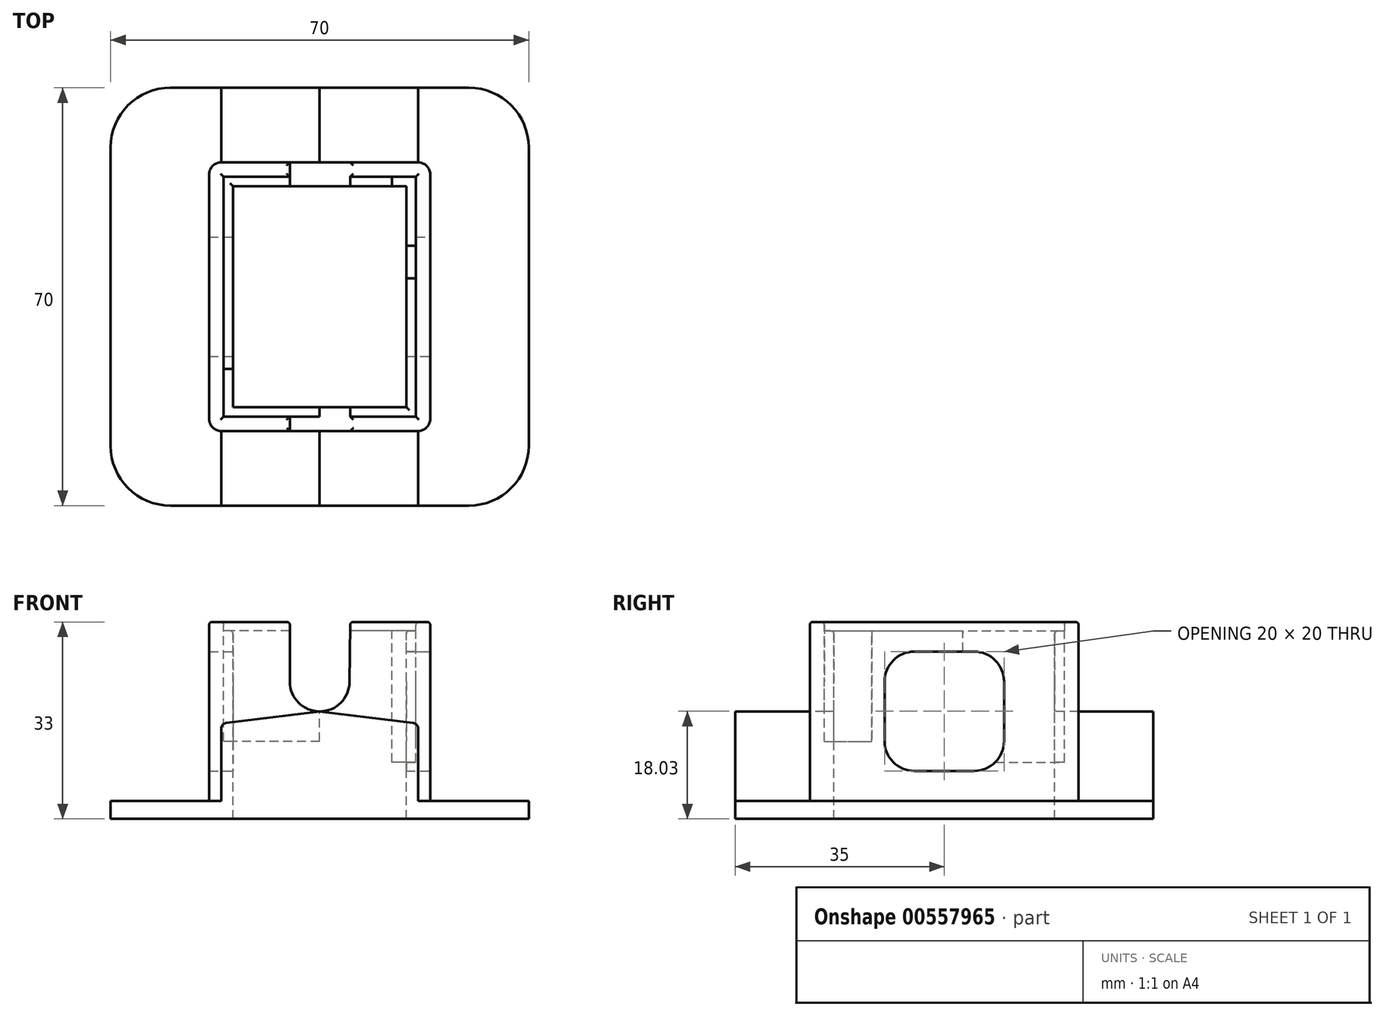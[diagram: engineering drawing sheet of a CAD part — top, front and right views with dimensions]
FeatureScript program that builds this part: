
annotation { "Feature Type Name" : "Feature", "Feature Type Description" : "" }
export const myFeature = defineFeature(function(context is Context, id is Id, definition is map)
    precondition{}
    {
        {
            var Q0;
            Q0=qCreatedBy(makeId("Top.planeOp"),FACE);
            var sketch = newSketch(context, id + "F0", { "sketchPlane" : qUnion([Q0])});
            skLineSegment(sketch, "E0.bottom", {"start": v(25, -35) * mm, "end": v(-25, -35) * mm});
            skLineSegment(sketch, "E0.top", {"start": v(25, 35) * mm, "end": v(-25, 35) * mm});
            skLineSegment(sketch, "E0.left", {"start": v(35, -25) * mm, "end": v(35, 25) * mm});
            skLineSegment(sketch, "E0.right", {"start": v(-35, -25) * mm, "end": v(-35, 25) * mm});
            skPoint(sketch, "E0.middle", {"position": v(0, 0) * mm});
            skPoint(sketch, "E1.visualSharp", {"position": v(-35, -35) * mm});
            skArc(sketch, "E1.filletArc", {"start": v(-35, -25) * mm, "mid": v(-32.07, -32.07) * mm, "end": v(-25, -35) * mm});
            skPoint(sketch, "E2.visualSharp", {"position": v(35, -35) * mm});
            skArc(sketch, "E2.filletArc", {"start": v(25, -35) * mm, "mid": v(32.07, -32.07) * mm, "end": v(35, -25) * mm});
            skPoint(sketch, "E3.visualSharp", {"position": v(35, 35) * mm});
            skArc(sketch, "E3.filletArc", {"start": v(35, 25) * mm, "mid": v(32.07, 32.07) * mm, "end": v(25, 35) * mm});
            skPoint(sketch, "E4.visualSharp", {"position": v(-35, 35) * mm});
            skArc(sketch, "E4.filletArc", {"start": v(-25, 35) * mm, "mid": v(-32.07, 32.07) * mm, "end": v(-35, 25) * mm});
            skSolve(sketch);
        }
        {
            var Q0;
            Q0=qSketchRegion(id+"F0",true);
            extrude(context, id + "F1", {"entities" : qUnion([Q0]), "depth" : 3 * mm, "offsetDistance" : 25 * mm});
        }
        {
            var Q0;
            Q0=makeQuery(id+"F1.opExtrude","CAP_FACE",FACE,{"disambiguationData":[OSD([sQuery(id+"F0.wireOp",EDGE,"E0.bottom"),sQuery(id+"F0.wireOp",EDGE,"E0.top"),sQuery(id+"F0.wireOp",EDGE,"E0.left"),sQuery(id+"F0.wireOp",EDGE,"E0.right"),sQuery(id+"F0.wireOp",EDGE,"E1.filletArc"),sQuery(id+"F0.wireOp",EDGE,"E2.filletArc"),sQuery(id+"F0.wireOp",EDGE,"E3.filletArc"),sQuery(id+"F0.wireOp",EDGE,"E4.filletArc")])],"isStart":false});
            var sketch = newSketch(context, id + "F2", { "sketchPlane" : qUnion([Q0])});
            skLineSegment(sketch, "E5.bottom", {"start": v(16.5, -22.5) * mm, "end": v(-16.5, -22.5) * mm});
            skLineSegment(sketch, "E5.top", {"start": v(16.5, 22.5) * mm, "end": v(-16.5, 22.5) * mm});
            skLineSegment(sketch, "E5.left", {"start": v(18.5, -20.5) * mm, "end": v(18.5, 20.5) * mm});
            skLineSegment(sketch, "E5.right", {"start": v(-18.5, -20.5) * mm, "end": v(-18.5, 20.5) * mm});
            skPoint(sketch, "E5.middle", {"position": v(0, 0) * mm});
            skPoint(sketch, "E6.visualSharp", {"position": v(18.5, -22.5) * mm});
            skArc(sketch, "E6.filletArc", {"start": v(16.5, -22.5) * mm, "mid": v(17.91, -21.91) * mm, "end": v(18.5, -20.5) * mm});
            skPoint(sketch, "E7.visualSharp", {"position": v(18.5, 22.5) * mm});
            skArc(sketch, "E7.filletArc", {"start": v(18.5, 20.5) * mm, "mid": v(17.91, 21.91) * mm, "end": v(16.5, 22.5) * mm});
            skPoint(sketch, "E8.visualSharp", {"position": v(-18.5, 22.5) * mm});
            skArc(sketch, "E8.filletArc", {"start": v(-16.5, 22.5) * mm, "mid": v(-17.91, 21.91) * mm, "end": v(-18.5, 20.5) * mm});
            skPoint(sketch, "E9.visualSharp", {"position": v(-18.5, -22.5) * mm});
            skArc(sketch, "E9.filletArc", {"start": v(-18.5, -20.5) * mm, "mid": v(-17.91, -21.91) * mm, "end": v(-16.5, -22.5) * mm});
            skSolve(sketch);
        }
        {
            var Q0;
            Q0=makeQuery(id+"F2.imprint","IMPRINT",FACE,{"disambiguationData":[TD([[makeQuery(id+"F2.imprint","IMPRINT",EDGE,{"derivedFrom":sQuery(id+"F2.wireOp",EDGE,"E5.bottom")}),-1.0]])]});
            extrude(context, id + "F3", {"entities" : qUnion([Q0]), "operationType" : NewBodyOperationType.ADD, "depth" : 30 * mm, "offsetDistance" : 25 * mm});
        }
        {
            var Q0;
            Q0=makeQuery(id+"F3.opExtrude","CAP_FACE",FACE,{"disambiguationData":[OSD([sQuery(id+"F2.wireOp",EDGE,"E5.bottom"),sQuery(id+"F2.wireOp",EDGE,"E5.top"),sQuery(id+"F2.wireOp",EDGE,"E5.left"),sQuery(id+"F2.wireOp",EDGE,"E5.right"),sQuery(id+"F2.wireOp",EDGE,"E6.filletArc"),sQuery(id+"F2.wireOp",EDGE,"E7.filletArc"),sQuery(id+"F2.wireOp",EDGE,"E8.filletArc"),sQuery(id+"F2.wireOp",EDGE,"E9.filletArc")])],"isStart":false});
            var sketch = newSketch(context, id + "F4", { "sketchPlane" : qUnion([Q0])});
            skLineSegment(sketch, "E10.bottom", {"start": v(-14.5, 18.5) * mm, "end": v(14.5, 18.5) * mm});
            skLineSegment(sketch, "E10.top", {"start": v(-14.5, -18.5) * mm, "end": v(14.5, -18.5) * mm});
            skLineSegment(sketch, "E10.left", {"start": v(-14.5, 18.5) * mm, "end": v(-14.5, -18.5) * mm});
            skLineSegment(sketch, "E10.right", {"start": v(14.5, 18.5) * mm, "end": v(14.5, -18.5) * mm});
            skPoint(sketch, "E10.middle", {"position": v(0, 0) * mm});
            skSolve(sketch);
        }
        {
            var Q0;
            Q0=makeQuery(id+"F4.imprint","IMPRINT",FACE,{"disambiguationData":[TD([[makeQuery(id+"F4.imprint","IMPRINT",EDGE,{"derivedFrom":sQuery(id+"F4.wireOp",EDGE,"E10.bottom")}),-1.0]])]});
            extrude(context, id + "F5", {"entities" : qUnion([Q0]), "operationType" : NewBodyOperationType.REMOVE, "endBound" : BoundingType.THROUGH_ALL, "oppositeDirection" : true, "depth" : 25 * mm});
        }
        {
            var Q0;
            Q0=makeQuery(id+"F3.opExtrude","CAP_FACE",FACE,{"disambiguationData":[OSD([sQuery(id+"F2.wireOp",EDGE,"E5.bottom"),sQuery(id+"F2.wireOp",EDGE,"E5.top"),sQuery(id+"F2.wireOp",EDGE,"E5.left"),sQuery(id+"F2.wireOp",EDGE,"E5.right"),sQuery(id+"F2.wireOp",EDGE,"E6.filletArc"),sQuery(id+"F2.wireOp",EDGE,"E7.filletArc"),sQuery(id+"F2.wireOp",EDGE,"E8.filletArc"),sQuery(id+"F2.wireOp",EDGE,"E9.filletArc")])],"isStart":false});
            var sketch = newSketch(context, id + "F6", { "sketchPlane" : qUnion([Q0])});
            skLineSegment(sketch, "E11.bottom", {"start": v(16.1, -20.1) * mm, "end": v(-16.1, -20.1) * mm});
            skLineSegment(sketch, "E11.top", {"start": v(16.1, 20.1) * mm, "end": v(-16.1, 20.1) * mm});
            skLineSegment(sketch, "E11.left", {"start": v(16.1, -20.1) * mm, "end": v(16.1, 20.1) * mm});
            skLineSegment(sketch, "E11.right", {"start": v(-16.1, -20.1) * mm, "end": v(-16.1, 20.1) * mm});
            skPoint(sketch, "E11.middle", {"position": v(0, 0) * mm});
            skSolve(sketch);
        }
        {
            var Q0;
            Q0=qSketchRegion(id+"F6",true);
            extrude(context, id + "F7", {"entities" : qUnion([Q0]), "operationType" : NewBodyOperationType.REMOVE, "oppositeDirection" : true, "depth" : 1.5 * mm});
        }
        {
            var Q0;
            Q0=makeQuery(id+"F7.boolean.opBoolean","COPY",FACE,{"derivedFrom":makeQuery(id+"F7.opExtrude","CAP_FACE",FACE,{"disambiguationData":[OSD([sQuery(id+"F6.wireOp",EDGE,"E11.bottom"),sQuery(id+"F6.wireOp",EDGE,"E11.top"),sQuery(id+"F6.wireOp",EDGE,"E11.left"),sQuery(id+"F6.wireOp",EDGE,"E11.right")])],"isStart":false})});
            var sketch = newSketch(context, id + "F8", { "sketchPlane" : qUnion([Q0])});
            skLineSegment(sketch, "E12.bottom", {"start": v(12.1, 20.1) * mm, "end": v(16.1, 20.1) * mm});
            skLineSegment(sketch, "E12.top", {"start": v(12.1, 3.1) * mm, "end": v(16.1, 3.1) * mm});
            skLineSegment(sketch, "E12.left", {"start": v(12.1, 20.1) * mm, "end": v(12.1, 3.1) * mm});
            skLineSegment(sketch, "E12.right", {"start": v(16.1, 20.1) * mm, "end": v(16.1, 3.1) * mm});
            skSolve(sketch);
        }
        {
            var Q0;
            {var subQ0=sQuery(id+"F8.wireOp",EDGE,"E12.right");var subQ1=sQuery(id+"F8.wireOp",EDGE,"E12.top");var subQ2=makeQuery(id+"F8.imprint","INTERSECT",VERTEX,{"derivedFrom":[subQ1,subQ0]});Q0=makeQuery(id+"F8.imprint","IMPRINT",FACE,{"disambiguationData":[TD([[makeQuery(id+"F8.imprint","IMPRINT",EDGE,{"disambiguationData":[TD([[subQ2,1.0]])],"derivedFrom":subQ1}),1.0]])]});}
            var Q1;
            {var subQ1=sQuery(id+"F8.wireOp",EDGE,"E12.bottom");Q1=makeQuery(id+"F8.imprint","IMPRINT",FACE,{"disambiguationData":[TD([[makeQuery(id+"F8.imprint","IMPRINT",EDGE,{"derivedFrom":subQ1}),1.0]])]});}
            extrude(context, id + "F9", {"entities" : qUnion([Q0, Q1]), "operationType" : NewBodyOperationType.REMOVE, "oppositeDirection" : true, "depth" : 22 * mm});
        }
        {
            var Q0;
            Q0=makeQuery(id+"F3.opExtrude","CAP_FACE",FACE,{"disambiguationData":[OSD([sQuery(id+"F2.wireOp",EDGE,"E5.bottom"),sQuery(id+"F2.wireOp",EDGE,"E5.top"),sQuery(id+"F2.wireOp",EDGE,"E5.left"),sQuery(id+"F2.wireOp",EDGE,"E5.right"),sQuery(id+"F2.wireOp",EDGE,"E6.filletArc"),sQuery(id+"F2.wireOp",EDGE,"E7.filletArc"),sQuery(id+"F2.wireOp",EDGE,"E8.filletArc"),sQuery(id+"F2.wireOp",EDGE,"E9.filletArc")])],"isStart":false});
            var sketch = newSketch(context, id + "F10", { "sketchPlane" : qUnion([Q0])});
            skLineSegment(sketch, "E13.bottom", {"start": v(0, -20.1) * mm, "end": v(-16.1, -20.1) * mm});
            skLineSegment(sketch, "E13.top", {"start": v(0, -12.1) * mm, "end": v(-16.1, -12.1) * mm});
            skLineSegment(sketch, "E13.left", {"start": v(0, -20.1) * mm, "end": v(0, -12.1) * mm});
            skLineSegment(sketch, "E13.right", {"start": v(-16.1, -20.1) * mm, "end": v(-16.1, -12.1) * mm});
            skSolve(sketch);
        }
        {
            var Q0;
            Q0=qSketchRegion(id+"F10",true);
            extrude(context, id + "F11", {"entities" : qUnion([Q0]), "operationType" : NewBodyOperationType.REMOVE, "oppositeDirection" : true, "depth" : 20 * mm, "offsetDistance" : 25 * mm});
        }
        {
            var Q0;
            Q0=makeQuery(id+"F3.opExtrude","SWEPT_FACE",FACE,{"disambiguationData":[OSD([sQuery(id+"F2.wireOp",EDGE,"E5.left")])]});
            var sketch = newSketch(context, id + "F12", { "sketchPlane" : qUnion([Q0])});
            skLineSegment(sketch, "E14.bottom", {"start": v(5, 8.03) * mm, "end": v(-5, 8.03) * mm});
            skLineSegment(sketch, "E14.top", {"start": v(5, 28.03) * mm, "end": v(-5, 28.03) * mm});
            skLineSegment(sketch, "E14.left", {"start": v(10, 13.03) * mm, "end": v(10, 23.03) * mm});
            skLineSegment(sketch, "E14.right", {"start": v(-10, 13.03) * mm, "end": v(-10, 23.03) * mm});
            skPoint(sketch, "E14.middle", {"position": v(0, 18.03) * mm});
            skPoint(sketch, "E15.visualSharp", {"position": v(10, 8.03) * mm});
            skArc(sketch, "E15.filletArc", {"start": v(5, 8.03) * mm, "mid": v(8.54, 9.5) * mm, "end": v(10, 13.03) * mm});
            skPoint(sketch, "E16.visualSharp", {"position": v(-10, 8.03) * mm});
            skArc(sketch, "E16.filletArc", {"start": v(-10, 13.03) * mm, "mid": v(-8.54, 9.5) * mm, "end": v(-5, 8.03) * mm});
            skPoint(sketch, "E17.visualSharp", {"position": v(-10, 28.03) * mm});
            skArc(sketch, "E17.filletArc", {"start": v(-5, 28.03) * mm, "mid": v(-8.54, 26.57) * mm, "end": v(-10, 23.03) * mm});
            skPoint(sketch, "E18.visualSharp", {"position": v(10, 28.03) * mm});
            skArc(sketch, "E18.filletArc", {"start": v(10, 23.03) * mm, "mid": v(8.54, 26.57) * mm, "end": v(5, 28.03) * mm});
            skSolve(sketch);
        }
        {
            var Q0;
            Q0=qSketchRegion(id+"F12",true);
            extrude(context, id + "F13", {"entities" : qUnion([Q0]), "operationType" : NewBodyOperationType.REMOVE, "endBound" : BoundingType.THROUGH_ALL, "oppositeDirection" : true, "depth" : 25 * mm, "offsetDistance" : 25 * mm, "hasSecondDirection" : true, "secondDirectionBound" : BoundingType.THROUGH_ALL, "secondDirectionOppositeDirection" : false, "secondDirectionDepth" : 25 * mm});
        }
        {
            var Q0;
            Q0=makeQuery(id+"F3.opExtrude","SWEPT_FACE",FACE,{"disambiguationData":[OSD([sQuery(id+"F2.wireOp",EDGE,"E5.bottom")])]});
            var sketch = newSketch(context, id + "F14", { "sketchPlane" : qUnion([Q0])});
            skArc(sketch, "E19", {"start": v(-5, 23) * mm, "mid": v(-0.03, 18) * mm, "end": v(5, 22.94) * mm});
            skLineSegment(sketch, "E20", {"start": v(-5, 23) * mm, "end": v(-5, 33) * mm});
            skLineSegment(sketch, "E21", {"start": v(-5, 33) * mm, "end": v(5.11, 33) * mm});
            skLineSegment(sketch, "E22", {"start": v(5.11, 33) * mm, "end": v(5, 22.94) * mm});
            skSolve(sketch);
        }
        {
            var Q0;
            Q0 = qSketchRegion(id + "F14", true);
            extrude(context, id + "F15", {"entities" : qUnion([Q0]), "operationType" : NewBodyOperationType.REMOVE, "endBound" : BoundingType.THROUGH_ALL, "oppositeDirection" : true, "depth" : 25 * mm, "offsetDistance" : 25 * mm});
        }
        {
            var Q0;
            Q0=makeQuery(id+"F3.opExtrude","SWEPT_FACE",FACE,{"disambiguationData":[OSD([sQuery(id+"F2.wireOp",EDGE,"E5.bottom")])]});
            var sketch = newSketch(context, id + "F16", { "sketchPlane" : qUnion([Q0])});
            skLineSegment(sketch, "E23.top", {"start": v(-16.5, 3) * mm, "end": v(16.5, 3) * mm});
            skLineSegment(sketch, "E23.left", {"start": v(-16.5, 15.97) * mm, "end": v(-16.5, 3) * mm});
            skLineSegment(sketch, "E23.right", {"start": v(16.5, 15.97) * mm, "end": v(16.5, 3) * mm});
            skLineSegment(sketch, "E24", {"start": v(0, 18) * mm, "end": v(16.5, 15.97) * mm});
            skLineSegment(sketch, "E25", {"start": v(0, 18) * mm, "end": v(-16.5, 15.97) * mm});
            skSolve(sketch);
        }
        {
            var Q0;
            Q0 = qSketchRegion(id + "F16", true);
            var Q1;
            Q1=makeQuery(id+"F1.opExtrude","SWEPT_FACE",FACE,{"disambiguationData":[OSD([sQuery(id+"F0.wireOp",EDGE,"E0.bottom")])]});
            extrude(context, id + "F17", {"entities" : qUnion([Q0]), "operationType" : NewBodyOperationType.ADD, "endBound" : BoundingType.UP_TO_SURFACE, "depth" : 25 * mm, "endBoundEntityFace" : qUnion([Q1]), "offsetDistance" : 25 * mm});
        }
        {
            var Q0;
            Q0=makeQuery(id+"F3.opExtrude","SWEPT_FACE",FACE,{"disambiguationData":[OSD([sQuery(id+"F2.wireOp",EDGE,"E5.top")])]});
            var sketch = newSketch(context, id + "F18", { "sketchPlane" : qUnion([Q0])});
            skLineSegment(sketch, "E26.top", {"start": v(-16.5, 3) * mm, "end": v(16.5, 3) * mm});
            skLineSegment(sketch, "E26.left", {"start": v(-16.5, 15.97) * mm, "end": v(-16.5, 3) * mm});
            skLineSegment(sketch, "E26.right", {"start": v(16.5, 15.97) * mm, "end": v(16.5, 3) * mm});
            skLineSegment(sketch, "E27", {"start": v(0, 18) * mm, "end": v(-16.5, 15.97) * mm});
            skLineSegment(sketch, "E28", {"start": v(0, 18) * mm, "end": v(16.5, 15.97) * mm});
            skSolve(sketch);
        }
        {
            var Q0;
            Q0 = qSketchRegion(id + "F18", true);
            var Q1;
            Q1=makeQuery(id+"F1.opExtrude","SWEPT_FACE",FACE,{"disambiguationData":[OSD([sQuery(id+"F0.wireOp",EDGE,"E0.top")])]});
            extrude(context, id + "F19", {"entities" : qUnion([Q0]), "operationType" : NewBodyOperationType.ADD, "endBound" : BoundingType.UP_TO_SURFACE, "depth" : 25 * mm, "endBoundEntityFace" : qUnion([Q1]), "offsetDistance" : 25 * mm});
        }
        {
            var Q0;
            {var subQ0=sQuery(id+"F2.wireOp",EDGE,"E7.filletArc");var subQ1=sQuery(id+"F2.wireOp",EDGE,"E5.bottom");var subQ2=sQuery(id+"F2.wireOp",EDGE,"E5.top");var subQ3=sQuery(id+"F2.wireOp",EDGE,"E5.left");var subQ4=sQuery(id+"F2.wireOp",EDGE,"E6.filletArc");Q0=makeQuery(id+"F15.boolean.opBoolean","SPLIT",FACE,{"disambiguationData":[TD([makeQuery(id+"F3.opExtrude","SWEPT_FACE",FACE,{"disambiguationData":[OSD([subQ3])]})])],"derivedFrom":makeQuery(id+"F3.opExtrude","CAP_FACE",FACE,{"disambiguationData":[OSD([subQ1,subQ2,subQ3,sQuery(id+"F2.wireOp",EDGE,"E5.right"),subQ4,subQ0,sQuery(id+"F2.wireOp",EDGE,"E8.filletArc"),sQuery(id+"F2.wireOp",EDGE,"E9.filletArc")])],"isStart":false})});}
            var Q1;
            {var subQ0=sQuery(id+"F2.wireOp",EDGE,"E9.filletArc");var subQ1=sQuery(id+"F2.wireOp",EDGE,"E5.bottom");var subQ2=sQuery(id+"F2.wireOp",EDGE,"E5.right");var subQ3=sQuery(id+"F2.wireOp",EDGE,"E5.top");var subQ4=sQuery(id+"F2.wireOp",EDGE,"E8.filletArc");Q1=makeQuery(id+"F15.boolean.opBoolean","SPLIT",FACE,{"disambiguationData":[TD([makeQuery(id+"F3.opExtrude","SWEPT_FACE",FACE,{"disambiguationData":[OSD([subQ2])]})])],"derivedFrom":makeQuery(id+"F3.opExtrude","CAP_FACE",FACE,{"disambiguationData":[OSD([subQ1,subQ3,sQuery(id+"F2.wireOp",EDGE,"E5.left"),subQ2,sQuery(id+"F2.wireOp",EDGE,"E6.filletArc"),sQuery(id+"F2.wireOp",EDGE,"E7.filletArc"),subQ4,subQ0])],"isStart":false})});}
            var Q2;
            Q2=makeQuery(id+"F7.boolean.opBoolean","INTERSECT",EDGE,{"derivedFrom":[makeQuery(id+"F5.boolean.opBoolean","COPY",FACE,{"derivedFrom":makeQuery(id+"F5.opExtrude","SWEPT_FACE",FACE,{"disambiguationData":[OSD([sQuery(id+"F4.wireOp",EDGE,"E10.right")])]})}),makeQuery(id+"F7.opExtrude","CAP_FACE",FACE,{"disambiguationData":[OSD([sQuery(id+"F6.wireOp",EDGE,"E11.bottom"),sQuery(id+"F6.wireOp",EDGE,"E11.top"),sQuery(id+"F6.wireOp",EDGE,"E11.left"),sQuery(id+"F6.wireOp",EDGE,"E11.right")])],"isStart":false})]});
            var Q3;
            Q3=makeQuery(id+"F7.boolean.opBoolean","INTERSECT",EDGE,{"derivedFrom":[makeQuery(id+"F5.boolean.opBoolean","COPY",FACE,{"derivedFrom":makeQuery(id+"F5.opExtrude","SWEPT_FACE",FACE,{"disambiguationData":[OSD([sQuery(id+"F4.wireOp",EDGE,"E10.top")])]})}),makeQuery(id+"F7.opExtrude","CAP_FACE",FACE,{"disambiguationData":[OSD([sQuery(id+"F6.wireOp",EDGE,"E11.bottom"),sQuery(id+"F6.wireOp",EDGE,"E11.top"),sQuery(id+"F6.wireOp",EDGE,"E11.left"),sQuery(id+"F6.wireOp",EDGE,"E11.right")])],"isStart":false})]});
            var Q4;
            Q4=makeQuery(id+"F7.boolean.opBoolean","INTERSECT",EDGE,{"derivedFrom":[makeQuery(id+"F5.boolean.opBoolean","COPY",FACE,{"derivedFrom":makeQuery(id+"F5.opExtrude","SWEPT_FACE",FACE,{"disambiguationData":[OSD([sQuery(id+"F4.wireOp",EDGE,"E10.left")])]})}),makeQuery(id+"F7.opExtrude","CAP_FACE",FACE,{"disambiguationData":[OSD([sQuery(id+"F6.wireOp",EDGE,"E11.bottom"),sQuery(id+"F6.wireOp",EDGE,"E11.top"),sQuery(id+"F6.wireOp",EDGE,"E11.left"),sQuery(id+"F6.wireOp",EDGE,"E11.right")])],"isStart":false})]});
            var Q5;
            {var subQ0=makeQuery(id+"F5.boolean.opBoolean","COPY",FACE,{"derivedFrom":makeQuery(id+"F5.opExtrude","SWEPT_FACE",FACE,{"disambiguationData":[OSD([sQuery(id+"F4.wireOp",EDGE,"E10.bottom")])]})});var subQ1=makeQuery(id+"F7.opExtrude","CAP_FACE",FACE,{"disambiguationData":[OSD([sQuery(id+"F6.wireOp",EDGE,"E11.bottom"),sQuery(id+"F6.wireOp",EDGE,"E11.top"),sQuery(id+"F6.wireOp",EDGE,"E11.left"),sQuery(id+"F6.wireOp",EDGE,"E11.right")])],"isStart":false});Q5=makeQuery(id+"F15.boolean.opBoolean","SPLIT",EDGE,{"disambiguationData":[TD([makeQuery(id+"F5.boolean.opBoolean","COPY",FACE,{"derivedFrom":makeQuery(id+"F5.opExtrude","SWEPT_FACE",FACE,{"disambiguationData":[OSD([sQuery(id+"F4.wireOp",EDGE,"E10.left")])]})})])],"derivedFrom":makeQuery(id+"F7.boolean.opBoolean","INTERSECT",EDGE,{"derivedFrom":[subQ0,subQ1]})});}
            var Q6;
            {var subQ0=makeQuery(id+"F5.boolean.opBoolean","COPY",FACE,{"derivedFrom":makeQuery(id+"F5.opExtrude","SWEPT_FACE",FACE,{"disambiguationData":[OSD([sQuery(id+"F4.wireOp",EDGE,"E10.bottom")])]})});var subQ1=makeQuery(id+"F7.opExtrude","CAP_FACE",FACE,{"disambiguationData":[OSD([sQuery(id+"F6.wireOp",EDGE,"E11.bottom"),sQuery(id+"F6.wireOp",EDGE,"E11.top"),sQuery(id+"F6.wireOp",EDGE,"E11.left"),sQuery(id+"F6.wireOp",EDGE,"E11.right")])],"isStart":false});Q6=makeQuery(id+"F15.boolean.opBoolean","SPLIT",EDGE,{"disambiguationData":[TD([makeQuery(id+"F9.boolean.opBoolean","COPY",FACE,{"derivedFrom":makeQuery(id+"F9.opExtrude","SWEPT_FACE",FACE,{"disambiguationData":[OSD([sQuery(id+"F8.wireOp",EDGE,"E12.left")])]})})])],"derivedFrom":makeQuery(id+"F7.boolean.opBoolean","INTERSECT",EDGE,{"derivedFrom":[subQ0,subQ1]})});}
            fillet(context, id + "F20", {"entities" : qUnion([Q0, Q1, Q2, Q3, Q4, Q5, Q6]), "radius" : 0.5 * mm, "tangentPropagation" : true, "allowEdgeOverflow" : false});
        }
        {
            var Q0;
            Q0=makeQuery(id+"F19.opExtrude","SWEPT_EDGE",EDGE,{"disambiguationData":[OSD([sQuery(id+"F2.wireOp",EDGE,"E5.top"),sQuery(id+"F2.wireOp",EDGE,"E7.filletArc"),sQuery(id+"F18.wireOp",EDGE,"E26.left"),sQuery(id+"F18.wireOp",EDGE,"E27")])]});
            var Q1;
            {var subQ0=sQuery(id+"F18.wireOp",EDGE,"E27");var subQ1=sQuery(id+"F2.wireOp",EDGE,"E5.top");Q1=makeQuery(id+"F19.opExtrude","TWEAK_EDGE",EDGE,{"derivedFrom":[makeQuery(id+"F1.opExtrude","SWEPT_FACE",FACE,{"disambiguationData":[OSD([sQuery(id+"F0.wireOp",EDGE,"E0.top")])]}),makeQuery(id+"F18.imprint","IMPRINT",EDGE,{"disambiguationData":[TD([[makeQuery(id+"F18.imprint","INTERSECT",VERTEX,{"derivedFrom":[makeQuery(id+"F15.boolean.opBoolean","INTERSECT",EDGE,{"derivedFrom":[makeQuery(id+"F3.opExtrude","SWEPT_FACE",FACE,{"disambiguationData":[OSD([subQ1])]}),makeQuery(id+"F15.opExtrude","SWEPT_FACE",FACE,{"disambiguationData":[OSD([sQuery(id+"F14.wireOp",EDGE,"E19")])]})]}),subQ0]}),-1.0]])],"derivedFrom":subQ0})]});}
            var Q2;
            {var subQ0=sQuery(id+"F18.wireOp",EDGE,"E28");var subQ1=sQuery(id+"F2.wireOp",EDGE,"E5.top");Q2=makeQuery(id+"F19.opExtrude","TWEAK_EDGE",EDGE,{"derivedFrom":[makeQuery(id+"F1.opExtrude","SWEPT_FACE",FACE,{"disambiguationData":[OSD([sQuery(id+"F0.wireOp",EDGE,"E0.top")])]}),makeQuery(id+"F18.imprint","IMPRINT",EDGE,{"disambiguationData":[TD([[makeQuery(id+"F18.imprint","INTERSECT",VERTEX,{"derivedFrom":[makeQuery(id+"F3.opExtrude","SWEPT_EDGE",EDGE,{"disambiguationData":[OSD([subQ1,sQuery(id+"F2.wireOp",EDGE,"E8.filletArc")])]}),sQuery(id+"F18.wireOp",EDGE,"E26.right"),subQ0]}),1.0]])],"derivedFrom":subQ0})]});}
            var Q3;
            Q3=makeQuery(id+"F19.opExtrude","SWEPT_EDGE",EDGE,{"disambiguationData":[OSD([sQuery(id+"F2.wireOp",EDGE,"E5.top"),sQuery(id+"F2.wireOp",EDGE,"E8.filletArc"),sQuery(id+"F18.wireOp",EDGE,"E26.right"),sQuery(id+"F18.wireOp",EDGE,"E28")])]});
            var Q4;
            Q4=makeQuery(id+"F19.opExtrude","TWEAK_EDGE",EDGE,{"derivedFrom":[makeQuery(id+"F1.opExtrude","SWEPT_FACE",FACE,{"disambiguationData":[OSD([sQuery(id+"F0.wireOp",EDGE,"E0.top")])]}),makeQuery(id+"F18.imprint","IMPRINT",EDGE,{"derivedFrom":sQuery(id+"F18.wireOp",EDGE,"E26.right")})]});
            var Q5;
            Q5=makeQuery(id+"F19.opExtrude","TWEAK_EDGE",EDGE,{"derivedFrom":[makeQuery(id+"F1.opExtrude","SWEPT_FACE",FACE,{"disambiguationData":[OSD([sQuery(id+"F0.wireOp",EDGE,"E0.top")])]}),makeQuery(id+"F18.imprint","IMPRINT",EDGE,{"derivedFrom":sQuery(id+"F18.wireOp",EDGE,"E26.left")})]});
            var Q6;
            Q6=makeQuery(id+"F19.opExtrude","SWEPT_EDGE",EDGE,{"disambiguationData":[OSD([sQuery(id+"F18.wireOp",EDGE,"E26.top"),sQuery(id+"F18.wireOp",EDGE,"E26.right")])]});
            var Q7;
            Q7=makeQuery(id+"F19.opExtrude","SWEPT_EDGE",EDGE,{"disambiguationData":[OSD([sQuery(id+"F18.wireOp",EDGE,"E26.top"),sQuery(id+"F18.wireOp",EDGE,"E26.left")])]});
            var Q8;
            Q8=makeQuery(id+"F3.opExtrude","CAP_EDGE",EDGE,{"disambiguationData":[OSD([sQuery(id+"F2.wireOp",EDGE,"E5.left")])],"isStart":true});
            var Q9;
            Q9=makeQuery(id+"F17.opExtrude","SWEPT_EDGE",EDGE,{"disambiguationData":[OSD([sQuery(id+"F16.wireOp",EDGE,"E23.top"),sQuery(id+"F16.wireOp",EDGE,"E23.right")])]});
            var Q10;
            Q10=makeQuery(id+"F17.opExtrude","SWEPT_EDGE",EDGE,{"disambiguationData":[OSD([sQuery(id+"F2.wireOp",EDGE,"E5.bottom"),sQuery(id+"F2.wireOp",EDGE,"E6.filletArc"),sQuery(id+"F16.wireOp",EDGE,"E23.right"),sQuery(id+"F16.wireOp",EDGE,"E24")])]});
            var Q11;
            Q11=makeQuery(id+"F17.opExtrude","SWEPT_EDGE",EDGE,{"disambiguationData":[OSD([sQuery(id+"F2.wireOp",EDGE,"E5.bottom"),sQuery(id+"F2.wireOp",EDGE,"E9.filletArc"),sQuery(id+"F16.wireOp",EDGE,"E23.left"),sQuery(id+"F16.wireOp",EDGE,"E25")])]});
            var Q12;
            Q12=makeQuery(id+"F17.opExtrude","TWEAK_EDGE",EDGE,{"derivedFrom":[makeQuery(id+"F1.opExtrude","SWEPT_FACE",FACE,{"disambiguationData":[OSD([sQuery(id+"F0.wireOp",EDGE,"E0.bottom")])]}),makeQuery(id+"F16.imprint","IMPRINT",EDGE,{"derivedFrom":sQuery(id+"F16.wireOp",EDGE,"E23.left")})]});
            var Q13;
            Q13=makeQuery(id+"F17.opExtrude","SWEPT_EDGE",EDGE,{"disambiguationData":[OSD([sQuery(id+"F16.wireOp",EDGE,"E23.top"),sQuery(id+"F16.wireOp",EDGE,"E23.left")])]});
            fillet(context, id + "F21", {"entities" : qUnion([Q0, Q1, Q2, Q3, Q4, Q5, Q6, Q7, Q8, Q9, Q10, Q11, Q12, Q13]), "radius" : 1 * mm, "tangentPropagation" : true, "allowEdgeOverflow" : false});
        }
    });
